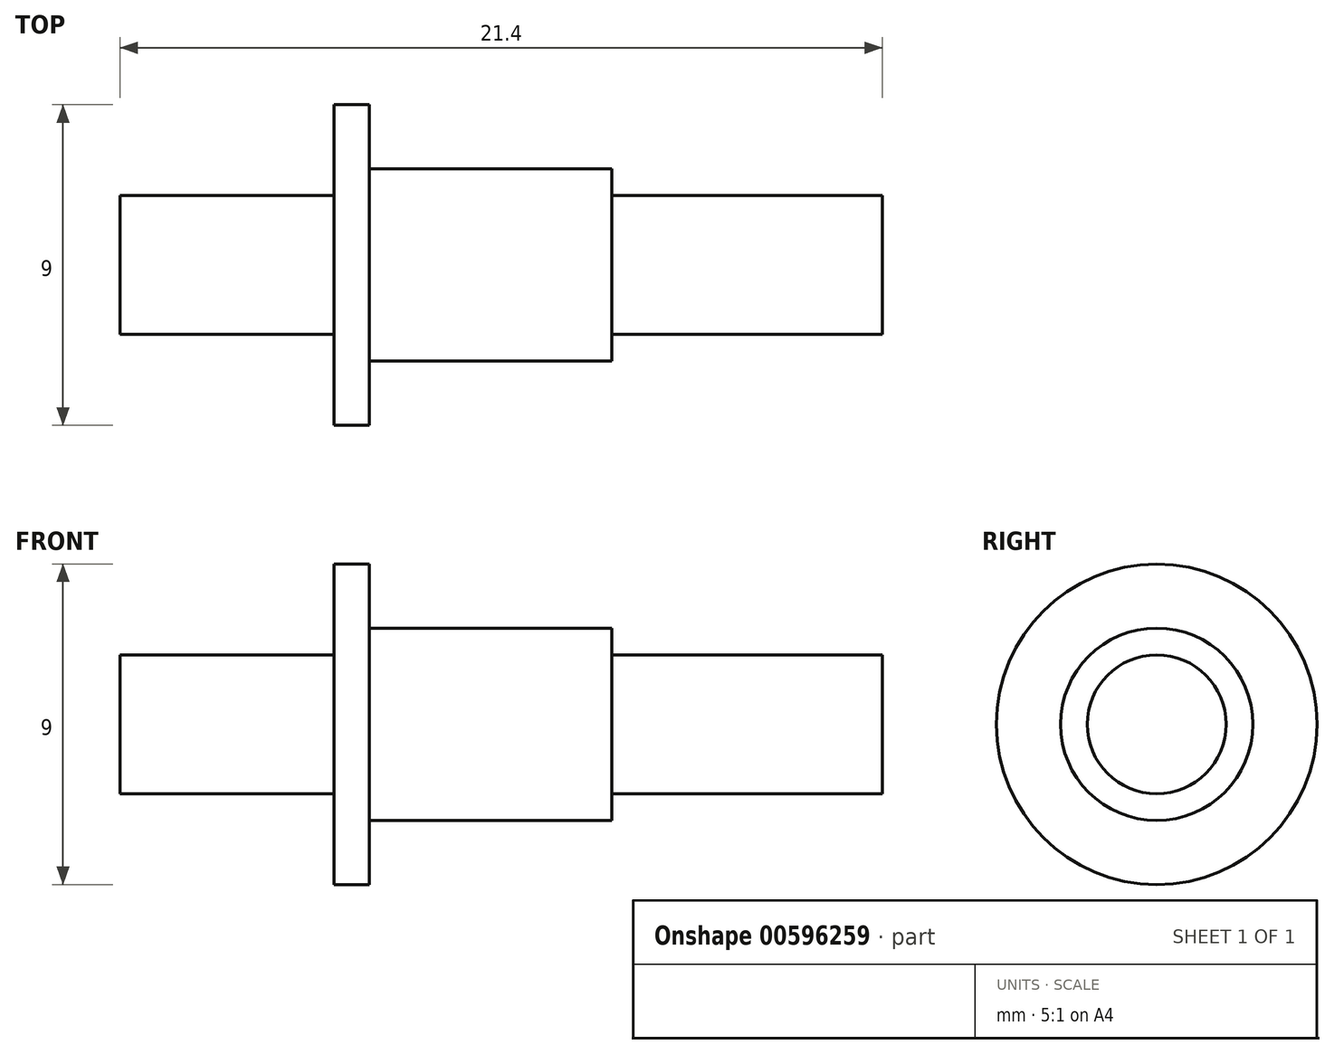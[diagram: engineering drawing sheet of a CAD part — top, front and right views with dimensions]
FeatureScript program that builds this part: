
annotation { "Feature Type Name" : "Feature", "Feature Type Description" : "" }
export const myFeature = defineFeature(function(context is Context, id is Id, definition is map)
    precondition{}
    {
        {
            var Q0;
            Q0=qCreatedBy(makeId("Front.planeOp"),FACE);
            var sketch = newSketch(context, id + "F0", { "sketchPlane" : qUnion([Q0])});
            skLineSegment(sketch, "E0", {"start": v(0, 0) * mm, "end": v(0, 1.95) * mm});
            skLineSegment(sketch, "E1", {"start": v(0, 1.95) * mm, "end": v(6, 1.95) * mm});
            skLineSegment(sketch, "E2", {"start": v(6, 1.95) * mm, "end": v(6, 4.5) * mm});
            skLineSegment(sketch, "E3", {"start": v(6, 4.5) * mm, "end": v(7, 4.5) * mm});
            skLineSegment(sketch, "E4", {"start": v(7, 4.5) * mm, "end": v(7, 2.7) * mm});
            skLineSegment(sketch, "E5", {"start": v(7, 2.7) * mm, "end": v(13.8, 2.7) * mm});
            skLineSegment(sketch, "E6", {"start": v(13.8, 2.7) * mm, "end": v(13.8, 1.95) * mm});
            skLineSegment(sketch, "E7", {"start": v(13.8, 1.95) * mm, "end": v(21.4, 1.95) * mm});
            skLineSegment(sketch, "E8", {"start": v(21.4, 1.95) * mm, "end": v(21.4, 0) * mm});
            skLineSegment(sketch, "E9", {"start": v(21.4, 0) * mm, "end": v(0, 0) * mm});
            skSolve(sketch);
        }
        {
            var Q0;
            Q0=makeQuery(id+"F0.imprint","IMPRINT",FACE,{"disambiguationData":[TD([[makeQuery(id+"F0.imprint","IMPRINT",EDGE,{"derivedFrom":sQuery(id+"F0.wireOp",EDGE,"E0")}),-1.0]])]});
            var Q1;
            Q1=sQuery(id+"F0.wireOp",EDGE,"E9");
            revolve(context, id + "F1", {"entities" : qUnion([Q0]), "axis" : qUnion([Q1]), "revolveType" : RevolveType.FULL});
        }
    });
